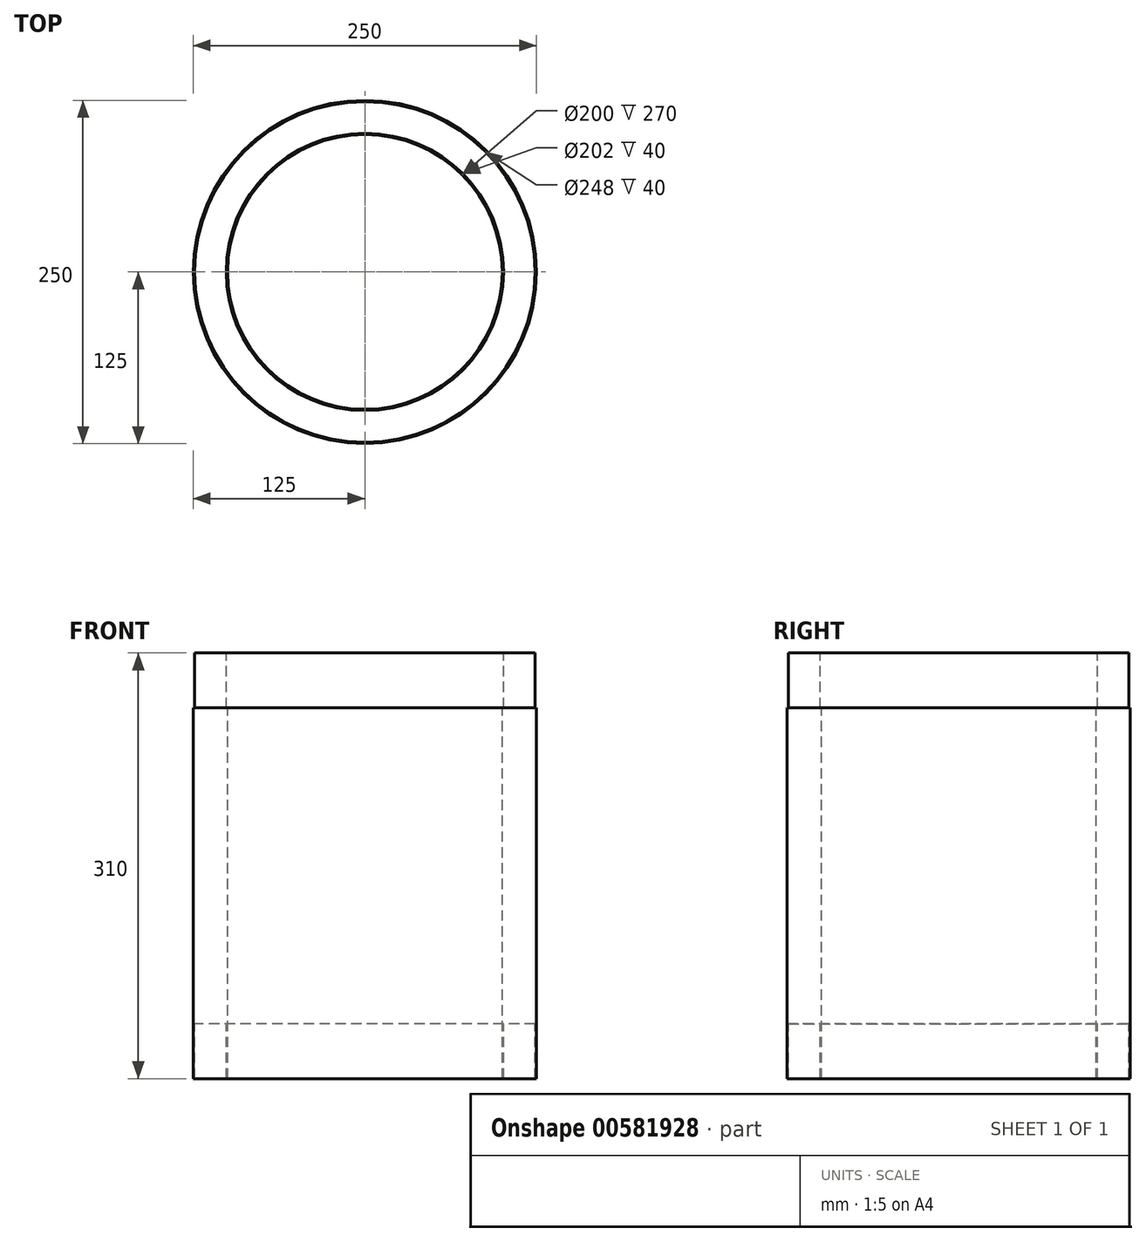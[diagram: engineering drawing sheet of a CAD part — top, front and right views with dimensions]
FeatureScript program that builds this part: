
annotation { "Feature Type Name" : "Feature", "Feature Type Description" : "" }
export const myFeature = defineFeature(function(context is Context, id is Id, definition is map)
    precondition{}
    {
        {
            var Q0;
            Q0=qCreatedBy(makeId("Front.planeOp"),FACE);
            var sketch = newSketch(context, id + "F0", { "sketchPlane" : qUnion([Q0])});
            skLineSegment(sketch, "E0", {"start": v(0, 345.75) * mm, "end": v(0, -558.03) * mm, "construction": true});
            skLineSegment(sketch, "E1", {"start": v(-100, -518.84) * mm, "end": v(-100, -248.84) * mm});
            skLineSegment(sketch, "E2", {"start": v(-100, -248.84) * mm, "end": v(-101, -248.84) * mm});
            skLineSegment(sketch, "E3", {"start": v(-101, -248.84) * mm, "end": v(-101, -208.84) * mm});
            skLineSegment(sketch, "E4", {"start": v(-101, -208.84) * mm, "end": v(-124, -208.84) * mm});
            skLineSegment(sketch, "E5", {"start": v(-124, -208.84) * mm, "end": v(-124, -248.84) * mm});
            skLineSegment(sketch, "E6", {"start": v(-124, -248.84) * mm, "end": v(-125, -248.84) * mm});
            skLineSegment(sketch, "E7", {"start": v(-125, -248.84) * mm, "end": v(-125, -518.84) * mm});
            skLineSegment(sketch, "E8", {"start": v(-125, -518.84) * mm, "end": v(-124, -518.84) * mm});
            skLineSegment(sketch, "E9", {"start": v(-124, -518.84) * mm, "end": v(-124, -478.84) * mm});
            skLineSegment(sketch, "E10", {"start": v(-124, -478.84) * mm, "end": v(-101, -478.84) * mm});
            skLineSegment(sketch, "E11", {"start": v(-101, -478.84) * mm, "end": v(-101, -518.84) * mm});
            skLineSegment(sketch, "E12", {"start": v(-101, -518.84) * mm, "end": v(-100, -518.84) * mm});
            skSolve(sketch);
        }
        {
            var Q0;
            Q0=qSketchRegion(id+"F0",true);
            var Q1;
            Q1=sQuery(id+"F0.wireOp",EDGE,"E0");
            revolve(context, id + "F1", {"entities" : qUnion([Q0]), "axis" : qUnion([Q1]), "revolveType" : RevolveType.FULL});
        }
    });
